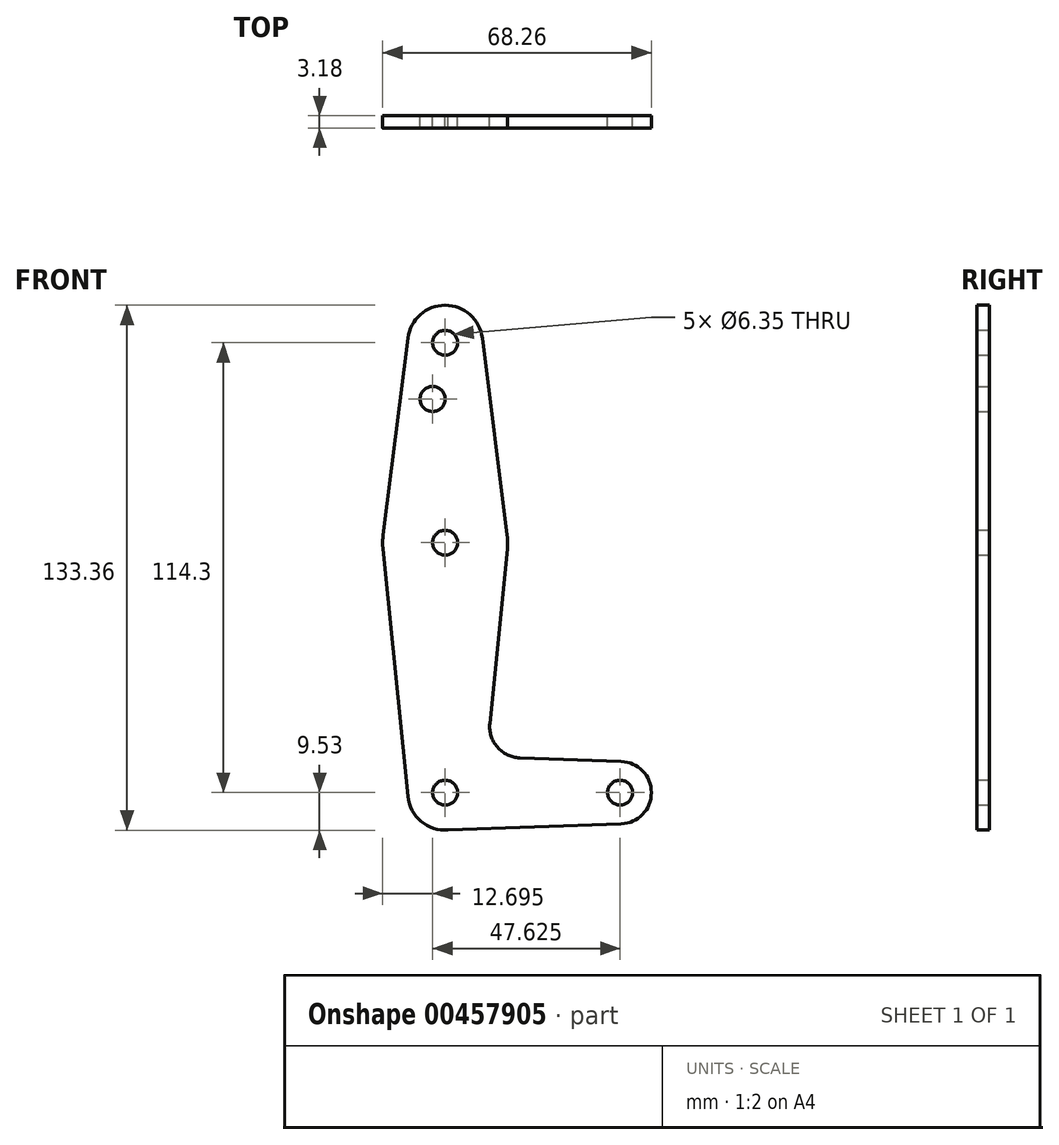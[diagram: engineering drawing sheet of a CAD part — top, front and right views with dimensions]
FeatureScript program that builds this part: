
annotation { "Feature Type Name" : "Feature", "Feature Type Description" : "" }
export const myFeature = defineFeature(function(context is Context, id is Id, definition is map)
    precondition{}
    {
        {
            var Q0;
            Q0=qCreatedBy(makeId("Front.planeOp"),FACE);
            var sketch = newSketch(context, id + "F0", { "sketchPlane" : qUnion([Q0])});
            skLineSegment(sketch, "E0", {"start": v(0, 0) * mm, "end": v(0, 114.3) * mm, "construction": true});
            skLineSegment(sketch, "E1", {"start": v(0, 0) * mm, "end": v(44.45, 0) * mm, "construction": true});
            skCircle(sketch, "E2", {"center": v(0, 114.3) * mm, "radius": 9.53 * mm});
            skCircle(sketch, "E3", {"center": v(44.45, 0) * mm, "radius": 7.94 * mm});
            skCircle(sketch, "E4", {"center": v(0, 0) * mm, "radius": 9.53 * mm});
            skCircle(sketch, "E5", {"center": v(0, 63.5) * mm, "radius": 15.88 * mm});
            skLineSegment(sketch, "E6", {"start": v(-9.45, 115.5) * mm, "end": v(-15.75, 65.48) * mm});
            skLineSegment(sketch, "E7", {"start": v(-15.8, 61.91) * mm, "end": v(-9.48, -0.95) * mm});
            skLineSegment(sketch, "E8", {"start": v(0, -9.53) * mm, "end": v(44.73, -7.93) * mm});
            skLineSegment(sketch, "E9", {"start": v(18.97, 8.85) * mm, "end": v(44.73, 7.93) * mm});
            skLineSegment(sketch, "E10.MirrorCS", {"start": v(9.45, 115.5) * mm, "end": v(15.75, 65.48) * mm});
            skLineSegment(sketch, "E11.MirrorCS", {"start": v(15.8, 61.91) * mm, "end": v(11.34, 17.59) * mm});
            skCircle(sketch, "E12", {"center": v(0, 114.3) * mm, "radius": 3.18 * mm});
            skCircle(sketch, "E13", {"center": v(0, 63.5) * mm, "radius": 3.18 * mm});
            skCircle(sketch, "E14", {"center": v(0, 0) * mm, "radius": 3.18 * mm});
            skCircle(sketch, "E15", {"center": v(44.45, 0) * mm, "radius": 3.18 * mm});
            skCircle(sketch, "E16", {"center": v(-3.18, 100.03) * mm, "radius": 3.18 * mm});
            skPoint(sketch, "E17.newPointB", {"position": v(9.48, -0.95) * mm});
            skArc(sketch, "E17.filletArc", {"start": v(11.34, 17.59) * mm, "mid": v(13.26, 11.57) * mm, "end": v(18.97, 8.85) * mm});
            skSolve(sketch);
        }
        {
            var Q0;
            Q0 = qSketchRegion(id + "F0", true);
            extrude(context, id + "F1", {"entities" : qUnion([Q0]), "depth" : 3.17 * mm});
        }
    });
